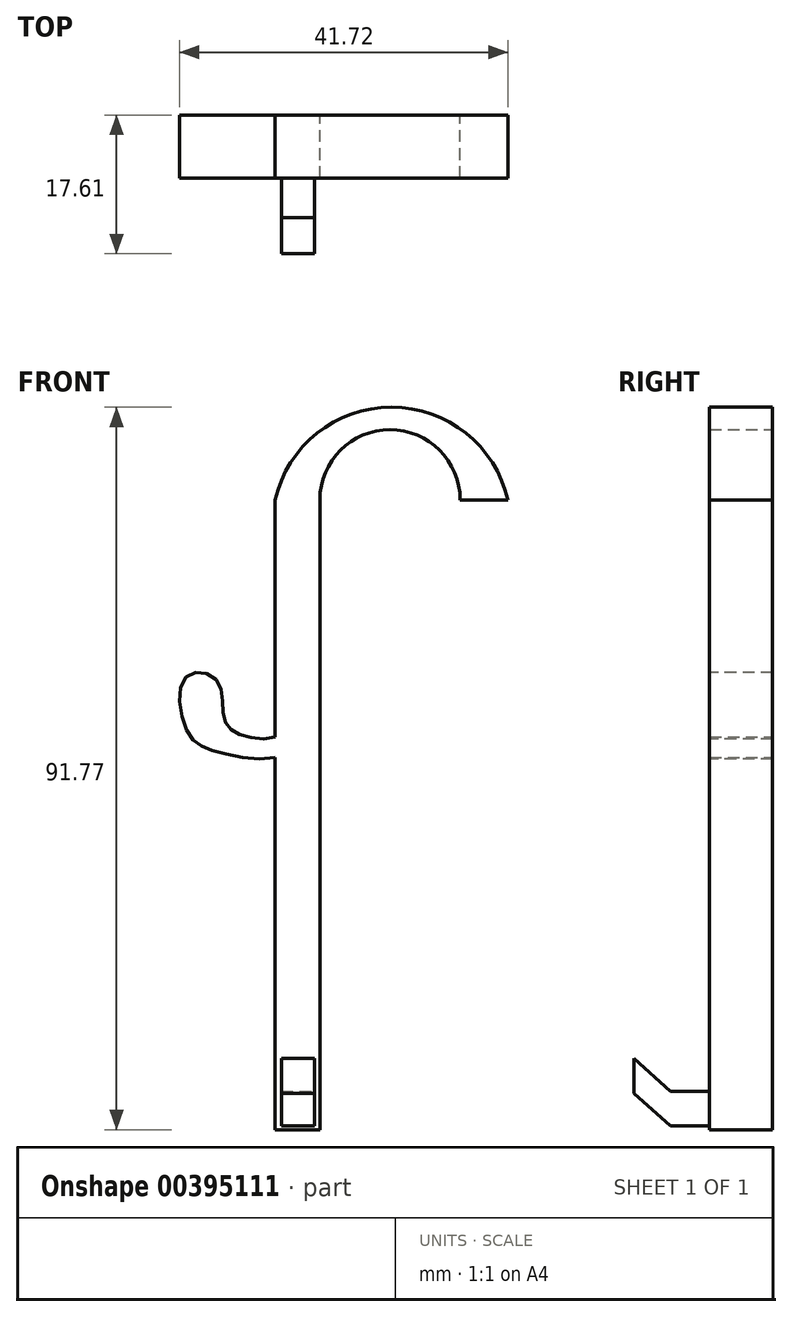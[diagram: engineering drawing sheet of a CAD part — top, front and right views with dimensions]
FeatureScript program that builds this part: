
annotation { "Feature Type Name" : "Feature", "Feature Type Description" : "" }
export const myFeature = defineFeature(function(context is Context, id is Id, definition is map)
    precondition{}
    {
        {
            var Q0;
            Q0=qCreatedBy(makeId("Front.planeOp"),FACE);
            var sketch = newSketch(context, id + "F0", { "sketchPlane" : qUnion([Q0])});
            skLineSegment(sketch, "E0.bottom", {"start": v(0, 23.51) * mm, "end": v(-5.7, 23.51) * mm});
            skLineSegment(sketch, "E0.top", {"start": v(0, 103.51) * mm, "end": v(-5.7, 103.51) * mm});
            skLineSegment(sketch, "E0.left", {"start": v(0, 23.51) * mm, "end": v(0, 103.51) * mm});
            skLineSegment(sketch, "E0.right", {"start": v(-5.7, 23.51) * mm, "end": v(-5.7, 70.78) * mm});
            skArc(sketch, "E1", {"start": v(17.82, 103.51) * mm, "mid": v(8.9, 112.42) * mm, "end": v(0, 103.51) * mm});
            skPoint(sketch, "E2.startSnap0", {"position": v(-2.85, 103.51) * mm});
            skArc(sketch, "E3", {"start": v(23.9, 103.51) * mm, "mid": v(9.1, 115.28) * mm, "end": v(-5.7, 103.51) * mm});
            skLineSegment(sketch, "E4", {"start": v(17.82, 103.51) * mm, "end": v(23.9, 103.51) * mm});
            skFitSpline(sketch, "E5", {"points": [v(-4.25, 77.23) * mm, v(-4.01, 71.93) * mm, v(-12.5, 71.39) * mm, v(-16.8, 74.04) * mm, v(-17.03, 80.97) * mm, v(-13.05, 80.58) * mm, v(-12.12, 75.6) * mm, v(-9.4, 73.5) * mm, v(-4.64, 74.2) * mm, v(-4.25, 77.23) * mm]});
            skLineSegment(sketch, "E6.trimOffspring", {"start": v(-5.7, 73.37) * mm, "end": v(-5.7, 103.51) * mm});
            skSolve(sketch);
        }
        {
            var Q0;
            Q0 = qSketchRegion(id + "F0", true);
            extrude(context, id + "F1", {"entities" : qUnion([Q0]), "depth" : 8 * mm});
        }
        {
            var Q0;
            Q0=makeQuery(id+"F1.opExtrude","CAP_FACE",FACE,{"disambiguationData":[OSD([sQuery(id+"F0.wireOp",EDGE,"E0.bottom"),sQuery(id+"F0.wireOp",EDGE,"E0.left"),sQuery(id+"F0.wireOp",EDGE,"E0.right"),sQuery(id+"F0.wireOp",EDGE,"E1"),sQuery(id+"F0.wireOp",EDGE,"E3"),sQuery(id+"F0.wireOp",EDGE,"E4")])],"isStart":false});
            var sketch = newSketch(context, id + "F2", { "sketchPlane" : qUnion([Q0])});
            skLineSegment(sketch, "E7.bottom", {"start": v(-4.88, 28.4) * mm, "end": v(-0.7, 28.4) * mm});
            skLineSegment(sketch, "E7.top", {"start": v(-4.88, 23.99) * mm, "end": v(-0.7, 23.99) * mm});
            skLineSegment(sketch, "E7.left", {"start": v(-4.88, 28.4) * mm, "end": v(-4.88, 23.99) * mm});
            skLineSegment(sketch, "E7.right", {"start": v(-0.7, 28.4) * mm, "end": v(-0.7, 23.99) * mm});
            skSolve(sketch);
        }
        {
            var Q0;
            Q0 = qSketchRegion(id + "F2", true);
            extrude(context, id + "F3", {"entities" : qUnion([Q0]), "operationType" : NewBodyOperationType.ADD, "depth" : 5 * mm});
        }
        {
            var Q0;
            Q0=makeQuery(id+"F3.opExtrude","CAP_FACE",FACE,{"disambiguationData":[OSD([sQuery(id+"F2.wireOp",EDGE,"E7.bottom"),sQuery(id+"F2.wireOp",EDGE,"E7.top"),sQuery(id+"F2.wireOp",EDGE,"E7.left"),sQuery(id+"F2.wireOp",EDGE,"E7.right")])],"isStart":false});
            var sketch = newSketch(context, id + "F4", { "sketchPlane" : qUnion([Q0])});
            skLineSegment(sketch, "E8.0", {"start": v(-4.88, 28.4) * mm, "end": v(-4.88, 23.99) * mm});
            skLineSegment(sketch, "E8.1", {"start": v(-4.88, 28.4) * mm, "end": v(-0.7, 28.4) * mm});
            skLineSegment(sketch, "E8.2", {"start": v(-0.7, 28.4) * mm, "end": v(-0.7, 23.99) * mm});
            skLineSegment(sketch, "E8.3", {"start": v(-4.88, 23.99) * mm, "end": v(-0.7, 23.99) * mm});
            skSolve(sketch);
        }
        {
            var Q0;
            Q0=makeQuery(id+"F3.opExtrude","SWEPT_FACE",FACE,{"disambiguationData":[OSD([sQuery(id+"F2.wireOp",EDGE,"E7.right")])]});
            var sketch = newSketch(context, id + "F5", { "sketchPlane" : qUnion([Q0])});
            skLineSegment(sketch, "E9", {"start": v(-13, 28.4) * mm, "end": v(-17.6, 32.54) * mm});
            skSolve(sketch);
        }
        {
            var Q0;
            Q0 = qSketchRegion(id + "F4", true);
            var Q1;
            Q1 = qConstructionFilter(qBodyType(qCreatedBy(id + "F5" ,EDGE), BodyType.WIRE), ConstructionObject.NO);
            sweep(context, id + "F6", {"operationType" : NewBodyOperationType.ADD, "profiles" : qUnion([Q0]), "path" : qUnion([Q1])});
        }
    });
